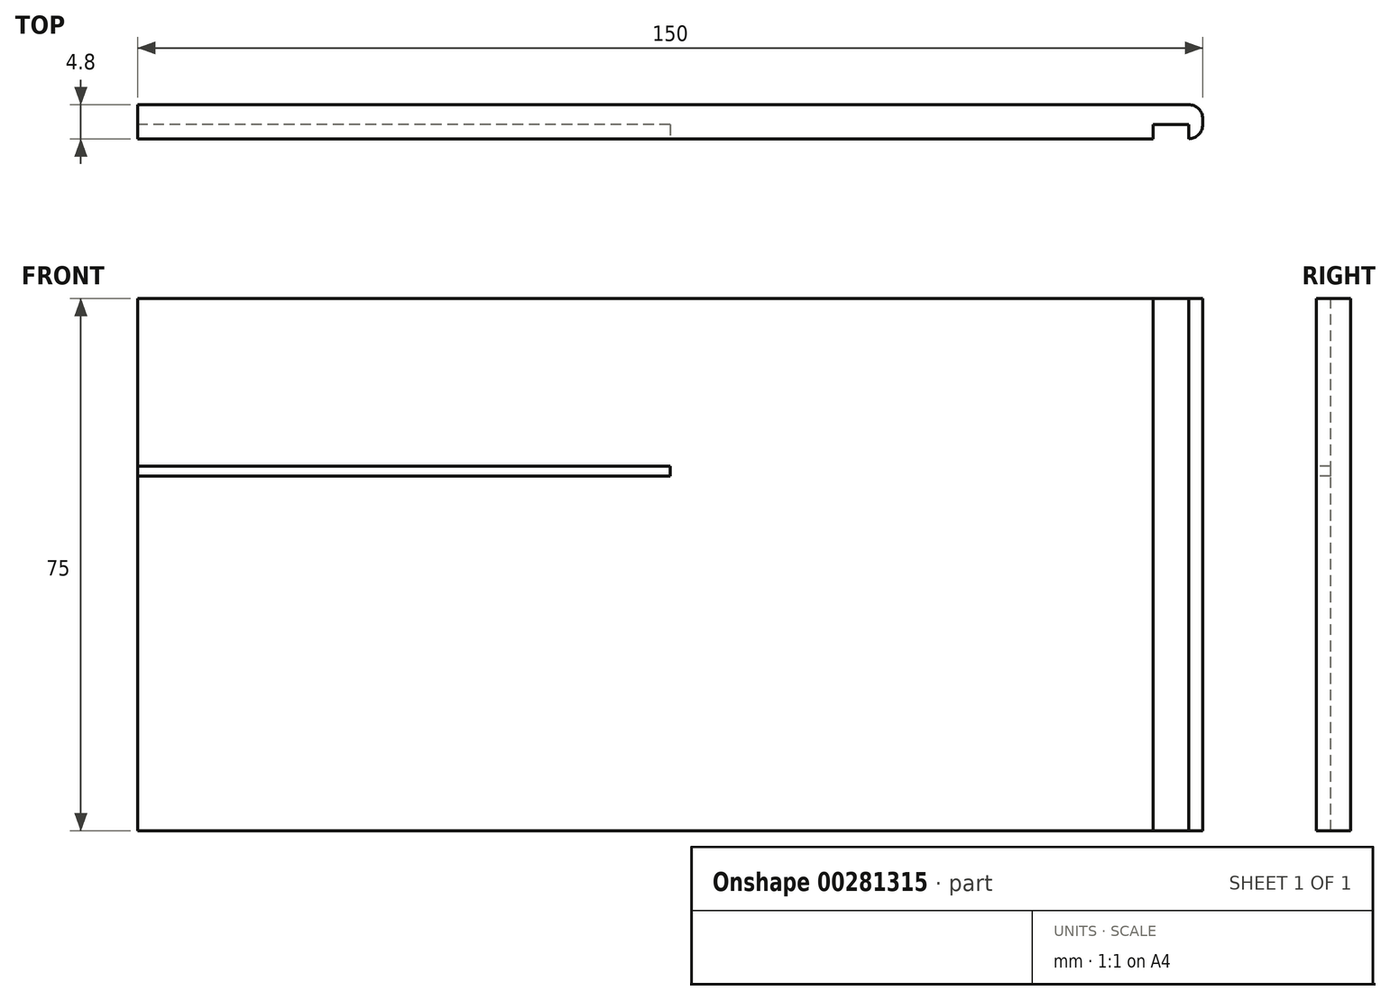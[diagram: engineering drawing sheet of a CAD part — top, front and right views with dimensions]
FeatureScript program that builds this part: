
annotation { "Feature Type Name" : "Feature", "Feature Type Description" : "" }
export const myFeature = defineFeature(function(context is Context, id is Id, definition is map)
    precondition{}
    {
        {
            var Q0;
            Q0=qCreatedBy(makeId("Front.planeOp"),FACE);
            var sketch = newSketch(context, id + "F0", { "sketchPlane" : qUnion([Q0])});
            skLineSegment(sketch, "E0.bottom", {"start": v(75, -37.5) * mm, "end": v(-75, -37.5) * mm});
            skLineSegment(sketch, "E0.top", {"start": v(75, 37.5) * mm, "end": v(-75, 37.5) * mm});
            skLineSegment(sketch, "E0.left", {"start": v(75, -37.5) * mm, "end": v(75, 37.5) * mm});
            skLineSegment(sketch, "E0.right", {"start": v(-75, -37.5) * mm, "end": v(-75, 37.5) * mm});
            skPoint(sketch, "E0.middle", {"position": v(0, 0) * mm});
            skSolve(sketch);
        }
        {
            var Q0;
            Q0 = qSketchRegion(id + "F0", true);
            extrude(context, id + "F1", {"entities" : qUnion([Q0]), "depth" : 4.8 * mm});
        }
        {
            var Q0;
            Q0=makeQuery(id+"F1.opExtrude","CAP_FACE",FACE,{"disambiguationData":[OSD([sQuery(id+"F0.wireOp",EDGE,"E0.bottom"),sQuery(id+"F0.wireOp",EDGE,"E0.top"),sQuery(id+"F0.wireOp",EDGE,"E0.left"),sQuery(id+"F0.wireOp",EDGE,"E0.right")])],"isStart":false});
            var sketch = newSketch(context, id + "F2", { "sketchPlane" : qUnion([Q0])});
            skLineSegment(sketch, "E1.bottom", {"start": v(68, -37.5) * mm, "end": v(73, -37.5) * mm});
            skLineSegment(sketch, "E1.top", {"start": v(68, 37.5) * mm, "end": v(73, 37.5) * mm});
            skLineSegment(sketch, "E1.left", {"start": v(68, -37.5) * mm, "end": v(68, 37.5) * mm});
            skLineSegment(sketch, "E1.right", {"start": v(73, -37.5) * mm, "end": v(73, 37.5) * mm});
            skPoint(sketch, "E1.middle", {"position": v(70.5, 0) * mm});
            skLineSegment(sketch, "E2.bottom", {"start": v(0, 13.9) * mm, "end": v(-75, 13.9) * mm});
            skLineSegment(sketch, "E2.top", {"start": v(0, 12.5) * mm, "end": v(-75, 12.5) * mm});
            skLineSegment(sketch, "E2.left", {"start": v(0, 13.9) * mm, "end": v(0, 12.5) * mm});
            skLineSegment(sketch, "E2.right", {"start": v(-75, 13.9) * mm, "end": v(-75, 12.5) * mm});
            skSolve(sketch);
        }
        {
            var Q0;
            Q0 = qSketchRegion(id + "F2", true);
            extrude(context, id + "F3", {"entities" : qUnion([Q0]), "operationType" : NewBodyOperationType.REMOVE, "oppositeDirection" : true, "depth" : 2 * mm});
        }
        {
            var Q0;
            Q0=makeQuery(id+"F1.opExtrude","CAP_EDGE",EDGE,{"disambiguationData":[OSD([sQuery(id+"F0.wireOp",EDGE,"E0.left")])],"isStart":true});
            var Q1;
            {var subQ0=sQuery(id+"F0.wireOp",EDGE,"E0.left");var subQ1=sQuery(id+"F0.wireOp",EDGE,"E0.top");var subQ3=makeQuery(id+"F1.opExtrude","CAP_EDGE",EDGE,{"disambiguationData":[OSD([subQ0])],"isStart":false});Q1=makeQuery(id+"F3.boolean.opBoolean","SPLIT",EDGE,{"disambiguationData":[TD([makeQuery(id+"F1.opExtrude","SWEPT_FACE",FACE,{"disambiguationData":[OSD([subQ1])]})])],"derivedFrom":subQ3});}
            fillet(context, id + "F4", {"entities" : qUnion([Q0, Q1]), "radius" : 2 * mm, "tangentPropagation" : true, "allowEdgeOverflow" : false});
        }
    });
